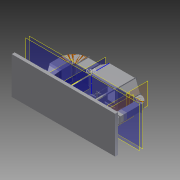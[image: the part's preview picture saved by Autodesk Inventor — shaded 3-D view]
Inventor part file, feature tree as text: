
AUTODESK INVENTOR PART (.ipt)
format: ipt  version: 2012 SP2 (Build 160219200, 219)  size: 1,349,632 bytes
history: native  units: in
note: dims shown in document units (in); Inventor stores cm internally (conversion verified against a paired STEP export)
features: sketch x59, extrude x57, projected_geometry x19, other x16, plane x8, loft x6, thicken_offset x5
ambient origin geometry x8: Origin, YZ Plane, XZ Plane, XY Plane, X Axis, Y Axis, Z Axis, Center Point
bodies: Solid1 (feature_tree)
feature tree (170):
  extrude  "Extrusion1"  Depth=0.125in
  extrude  "Extrusion2"  Depth=2.5in
  extrude  "Extrusion3"  Depth=2.5in
  extrude  "Extrusion4"  Depth=0.125in
  extrude  "Extrusion5"  Depth=0.125in
  extrude  "Extrusion6"  Depth=0.125in
  extrude  "Extrusion7"  Depth=0.125in
  extrude  "Extrusion8"  Depth=2.5in
  extrude  "Extrusion9"  Depth=2.5in
  extrude  "Extrusion10"  Depth=2.5in
  extrude  "Extrusion11"  Depth=2.5in
  extrude  "Extrusion12"  Depth=36.0in
  extrude  "Extrusion13"  Depth=61.5in TaperAngle=0.0deg
  extrude  "Extrusion14"  Depth=10.0in
  extrude  "Extrusion15"  Depth=2.5in
  extrude  "Extrusion18"  Depth=0.125in TaperAngle=0.0deg
  extrude  "Extrusion19"  Depth=0.125in TaperAngle=0.0deg
  extrude  "Extrusion20"  Depth=0.125in TaperAngle=0.0deg
  extrude  "Extrusion21"  Depth=2.5in
  extrude  "Extrusion22"  Depth=2.5in
  extrude  "Extrusion23"  Depth=0.125in TaperAngle=0.0deg
  sketch  "Sketch25"  dims[d56=2.5in d57=0.125in d58=0.0in]
  plane  "Work Plane1"
  plane  "Work Plane2"
  plane  "Work Plane3"
  loft  "Loft2"
  plane  "Work Plane4"
  extrude  "Extrusion30"  Depth=0.125in TaperAngle=0.0deg
  extrude  "Extrusion31"  Depth=0.125in TaperAngle=0.0deg
  extrude  "Extrusion32"  Depth=0.125in TaperAngle=0.0deg
  extrude  "Extrusion33"  Depth=2.5in
  extrude  "Extrusion34"  Depth=2.5in
  plane  "Work Plane5"
  extrude  "Extrusion35"  Depth=0.125in TaperAngle=0.0deg
  extrude  "Extrusion36"  Depth=20.0in
  extrude  "Extrusion37"  Depth=96.0in
  sketch  "Sketch44"  dims[d83=33.5in d84=0.125in d85=0.0in]
  extrude  "Extrusion40"  Depth=2.0in
  plane  "Work Plane6"
  sketch  "Sketch48"  dims[d96=36.0in d97=0.0in d98=0.125in d99=0.0in]
  extrude  "Extrusion43"  Depth=0.125in TaperAngle=0.0deg
  extrude  "Extrusion44"  Depth=0.125in
  extrude  "Extrusion45"  Depth=0.125in TaperAngle=0.0deg
  extrude  "Extrusion46"  Depth=6.0in
  extrude  "Extrusion47"  Depth=6.0in
  extrude  "Extrusion48"  Depth=6.0in
  extrude  "Extrusion49"  Depth=6.0in
  extrude  "Extrusion50"  Depth=0.125in TaperAngle=0.0deg
  extrude  "Extrusion52"  Depth=2.0in
  extrude  "Extrusion53"  Depth=2.0in
  extrude  "Extrusion54"  Depth=0.25in TaperAngle=0.0deg
  extrude  "Extrusion55"  Depth=12.5in
  extrude  "Extrusion56"  Depth=21.0in
  thicken_offset  "Thicken8"
  thicken_offset  "Thicken9"
  thicken_offset  "Thicken10"
  thicken_offset  "Thicken11"
  thicken_offset  "Thicken12"
  extrude  "Extrusion57"  Depth=12.0in
  extrude  "Extrusion58"  Depth=12.0in
  plane  "Work Plane7"
  extrude  "Extrusion59"  TaperAngle=0.0deg  [1 undecoded]
  extrude  "Extrusion60"  Depth=12.0in
  extrude  "Extrusion61"  Depth=10.125in
  extrude  "Extrusion62"  Depth=0.125in
  extrude  "Extrusion63"  Depth=0.125in
  plane  "Work Plane8"
  extrude  "Extrusion64"  Depth=49.5in TaperAngle=0.0deg
  extrude  "Extrusion65"  Depth=2.0in
  extrude  "Extrusion66"  Depth=2.0in
  extrude  "Extrusion67"  Depth=0.125in
  extrude  "Extrusion68"  Depth=0.125in
  extrude  "Extrusion69"  Depth=47.5in TaperAngle=0.0deg
  extrude  "Extrusion70"  Depth=2.0in
  sketch  "Sketch1"  dims[d0=52.0in d1=36.0in d2=0.125in d3=0.125in]
  sketch  "Sketch2"  dims[d4=2.5in d5=2.5in d6=2.5in d7=2.5in]
  projected_geometry  "Projected Loop1"
  sketch  "Sketch3"  dims[d8=2.5in d9=2.5in d10=2.5in d11=2.5in]
  projected_geometry  "Projected Loop2"
  sketch  "Sketch4"  dims[d12=36.0in d14=0.125in]
  projected_geometry  "Projected Loop3"
  sketch  "Sketch5"  dims[d15=0.125in d16=0.125in]
  projected_geometry  "Projected Loop4"
  sketch  "Sketch6"  dims[d17=0.125in d18=0.125in]
  sketch  "Sketch7"  dims[d19=0.125in d20=0.125in]
  sketch  "Sketch8"  dims[d21=2.5in d22=2.5in]
  projected_geometry  "Projected Loop5"
  sketch  "Sketch9"  dims[d23=2.5in d24=2.5in]
  projected_geometry  "Projected Loop6"
  sketch  "Sketch10"  dims[d25=2.5in d26=2.5in]
  projected_geometry  "Projected Loop7"
  sketch  "Sketch11"  dims[d27=2.5in d28=2.5in]
  projected_geometry  "Projected Loop8"
  sketch  "Sketch12"  dims[d29=52.0in d30=36.0in]
  sketch  "Sketch13"  dims[d31=52.0in d32=61.5in d33=0.0in]
  sketch  "Sketch14"  dims[d34=2.5in d35=10.0in]
  sketch  "Sketch15"  dims[d36=0.125in d37=0.0in d38=2.5in]
  sketch  "Sketch18"  dims[d39=10.0in d40=0.125in d41=0.0in]
  sketch  "Sketch19"  dims[d42=2.5in d43=0.125in d44=0.0in]
  sketch  "Sketch20"  dims[d45=2.5in d46=0.125in d47=0.0in]
  sketch  "Sketch21"  dims[d48=0.125in d49=0.0in d50=2.5in]
  sketch  "Sketch22"  dims[d51=2.5in d52=2.5in]
  sketch  "Sketch23"  dims[d53=2.5in d54=0.125in d55=0.0in]
  sketch  "Sketch33"  dims[d59=2.5in d60=0.125in d61=0.0in]
  other  "Edges3"
  sketch  "Sketch35"  dims[d62=2.5in d63=0.125in d64=0.0in]
  sketch  "Sketch36"  dims[d65=2.5in d66=0.125in d67=0.0in]
  sketch  "Sketch37"  dims[d68=0.125in d69=0.0in d70=2.5in]
  sketch  "Sketch38"  dims[d71=2.5in d72=2.5in]
  sketch  "Sketch39"  dims[d73=2.5in d74=0.125in d75=0.0in]
  sketch  "Sketch40"  dims[d76=20.0in d77=20.0in]
  sketch  "Sketch41"  dims[d78=64.0in d79=96.0in]
  sketch  "Sketch43"  dims[d80=6.0in d81=0.0in d82=2.0in]
  sketch  "Sketch46"  dims[d94=0.125in d95=0.125in]
  other  "Srf2"
  other  "Edges6"
  other  "Edges7"
  sketch  "Sketch51"  dims[d102=6.0in d103=6.0in]
  other  "Edges10"
  other  "Edges11"
  other  "Srf4"
  sketch  "Sketch52"  dims[d104=15.0in d105=6.0in]
  projected_geometry  "Projected Loop11"
  sketch  "Sketch53"  dims[d106=0.125in d107=0.0in d108=6.0in]
  other  "Edges13"
  other  "Edges14"
  other  "Srf5"
  sketch  "Sketch54"  dims[d110=15.0in d111=6.0in]
  sketch  "Sketch55"  dims[d112=24.0in d113=0.125in d114=0.0in]
  sketch  "Sketch56"  dims[d115=0.125in d116=0.0in d117=2.0in]
  sketch  "Sketch57"  dims[d118=2.0in d119=2.0in]
  sketch  "Sketch58"  dims[d120=2.0in d121=0.25in d122=0.0in]
  other  "Edges15"
  other  "Edges16"
  other  "Srf6"
  sketch  "Sketch59"  dims[d126=0.125in d135=12.5in]
  sketch  "Sketch60"  dims[d149=12.5in d177=21.0in]
  sketch  "Sketch61"  dims[d178=12.0in d179=12.0in]
  projected_geometry  "Projected Loop12"
  other  "Edges17"
  other  "Edges18"
  other  "Srf7"
  sketch  "Sketch62"  dims[d180=12.0in d181=12.0in]
  projected_geometry  "Projected Loop13"
  sketch  "Sketch63"  dims[d182=0.0in d183=90.0deg d184=0.0in d185=90.0deg]
  sketch  "Sketch64"  dims[d186=23.0in d193=12.0in]
  projected_geometry  "Projected Loop14"
  projected_geometry  "Projected Loop15"
  sketch  "Sketch66"  dims[d194=12.0in d195=10.125in]
  sketch  "Sketch67"  dims[d196=12.0in d197=0.125in]
  sketch  "Sketch68"  dims[d198=0.125in d199=0.125in]
  sketch  "Sketch69"  dims[d200=0.125in d201=49.5in d202=0.0in]
  sketch  "Sketch70"  dims[d203=2.0in d204=2.0in]
  projected_geometry  "Projected Loop16"
  projected_geometry  "Projected Loop17"
  projected_geometry  "Projected Loop18"
  sketch  "Sketch71"  dims[d205=2.0in d206=2.0in]
  sketch  "Sketch72"  dims[d207=0.25in d208=0.0in d209=0.125in]
  sketch  "Sketch74"  dims[d210=0.125in d211=0.125in]
  projected_geometry  "Projected Loop20"
  projected_geometry  "Projected Loop21"
  sketch  "Sketch75"  dims[d212=0.125in d213=47.5in d214=0.0in]
  sketch  "Sketch76"  dims[d215=2.0in d216=2.0in]
  projected_geometry  "Projected Loop22"
  sketch  "Sketch77"  dims[d217=2.0in d218=2.0in d219=0.25in d220=0.0in d221=0.125in d222=0.125in d223=0.125in d224=0.125in d225=28.5in d226=0.0in d227=30.0in d228=12.0in d229=43.0in d230=9.5in d231=25.0in d232=0.125in d233=0.0in d234=0.125in d235=0.125in d236=11.75in d237=0.0in d238=0.125in d239=0.0in d240=2.0in d241=2.0in d242=2.0in d243=2.0in d256=2.0in d257=2.0in d258=2.0in d259=2.0in d260=0.25in d261=0.0in d268=42.75in d269=2.0in d270=2.0in d271=2.0in d272=2.0in d275=0.25in d276=0.0in d277=0.25in d278=0.0in d279=0.3937in d280=90.0deg d281=0.3937in d282=90.0deg d290=2.0in d291=2.0in d292=2.0in d293=2.0in d294=0.25in d295=0.0in d296=0.3937in d297=90.0deg d298=0.3937in d299=90.0deg d306=6.0in d307=6.0in d308=24.0in d309=24.0in d310=2.0in d311=2.0in d312=2.0in d313=2.0in d314=0.25in d315=0.0in d316=0.125in d317=0.125in d318=0.125in d319=0.125in d320=24.0in d321=0.0in d322=0.0in d323=90.0deg d324=0.0in d325=90.0deg d326=2.0in d327=2.0in d328=2.0in d329=2.0in d330=0.25in d331=0.0in d332=43.25in d333=18.25in d334=24.0in d335=0.125in d336=0.0in d337=0.125in d338=0.125in d339=23.875in d340=0.0in d343=0.125in d344=0.0in d345=2.0in d346=2.0in d347=2.0in d348=2.0in d349=0.25in d350=0.0in d351=0.3937in d352=90.0deg d353=0.3937in d354=90.0deg d355=24.0in d356=6.5in d357=27.0in d358=9.5in d359=0.0in d360=5.5in d361=20.5in d362=24.0in d363=26.0in d364=0.0in d365=2.0in d366=2.0in d367=2.0in d368=9.5in d369=24.0in d370=0.0in d371=0.0in d372=90.0deg d373=0.0in d374=90.0deg d395=0.1in d396=0.1in d397=0.1in d398=0.1in d399=0.1in d400=0.1in d401=0.1in d402=0.1in d403=0.1in d404=0.1in d405=1.625in d406=1.625in d407=11.5in d408=11.5in d409=1.625in d410=1.625in d411=1.0in d412=0.0in d414=0.5in d415=0.8125in d416=0.8125in d417=0.5in d418=0.8125in d419=0.8125in d420=50.5in d421=0.0in d422=33.25in d423=4.0in d424=1.1875in d425=40.0in d426=2.125in d427=0.25in d428=0.0in d431=4.5in d432=4.5in d433=4.5in d434=1.5in d435=0.25in d436=0.0in d441=8.25in d442=10.5in d443=10.5in d444=3.75in d445=0.25in d446=0.0in d447=15.0in d448=15.0in d449=2.25in d450=2.25in d451=0.25in d452=0.0in d453=2.25in d454=10.5in d455=10.5in d456=2.25in d457=0.25in d458=0.0in d459=40.0in d460=27.0in d461=18.0in d462=7.0in d463=1.875in d464=0.25in d465=0.0in d466=2.0in d467=0.375in d468=1.0in d469=4.25in d470=0.375in d471=4.25in d472=1.0in d473=2.0in d474=3.675in d475=0.0in d476=4.0in d477=2.0in d478=2.0in d479=4.0in d480=0.325in d481=0.0in d482=2.0in d483=1.25in d484=2.0in d485=1.25in d486=0.25in d487=0.0in d488=0.25in d489=0.25in d490=2.25in d491=0.0in d492=0.25in d493=0.25in d494=1.0in d495=2.25in d496=0.0in d497=0.25in d498=2.0002in d499=2.0in d500=2.0in d501=2.0in d502=0.25in d503=0.0in]
  loft  "LoftSrf2"
  loft  "LoftSrf4"
  loft  "LoftSrf5"
  loft  "LoftSrf6"
  loft  "LoftSrf7"
note: 1 required parameter value undecoded (feature->parameter linkage not recoverable at this tier; creation-order binding heuristic only, values carry confidence <= 0.55)
